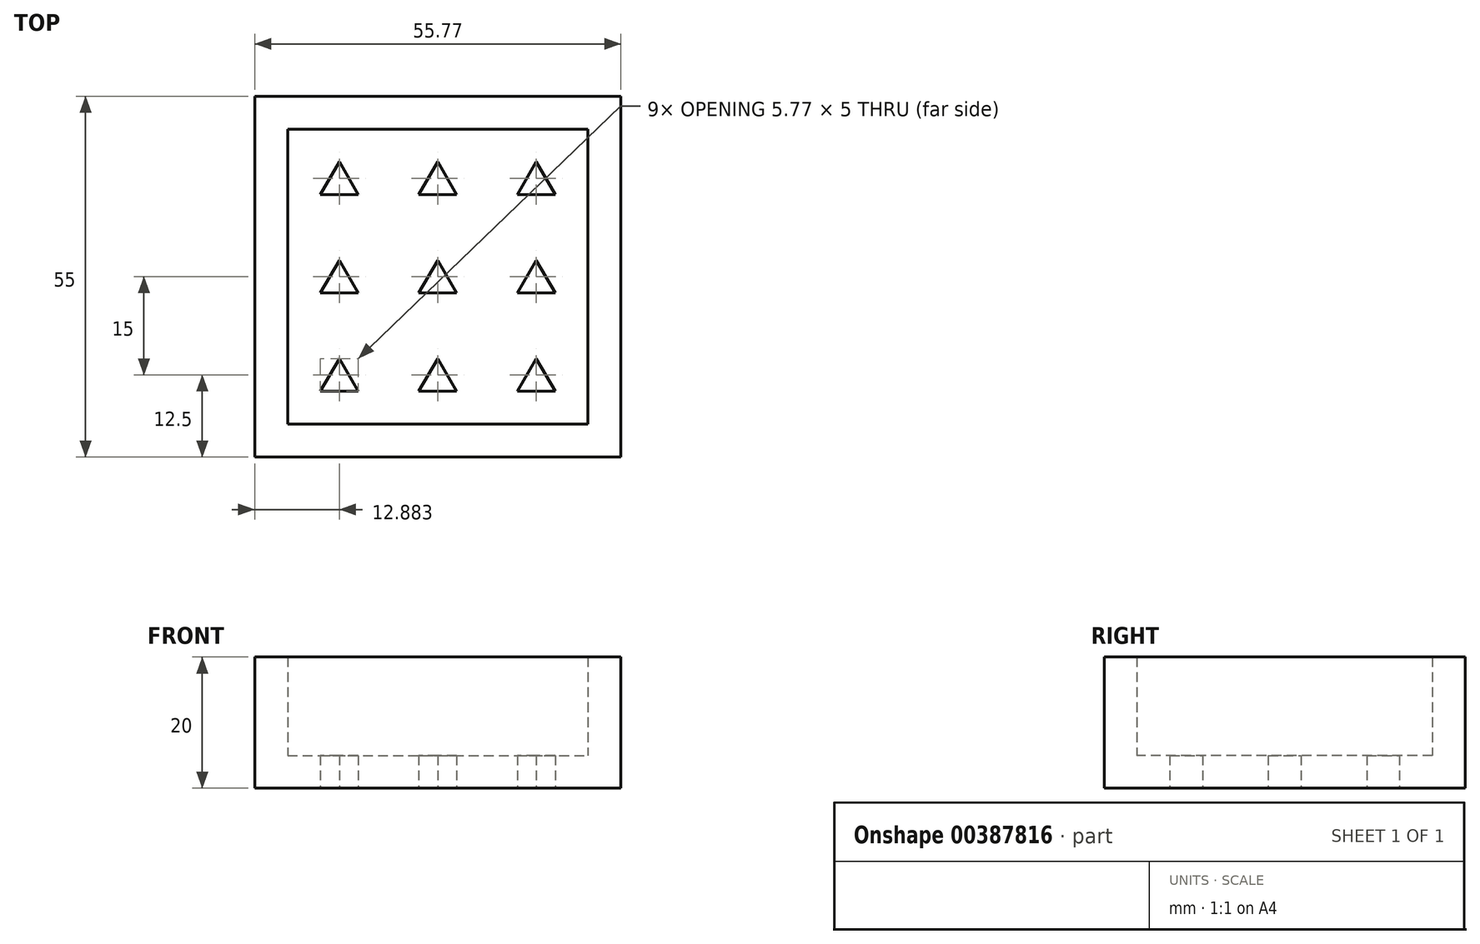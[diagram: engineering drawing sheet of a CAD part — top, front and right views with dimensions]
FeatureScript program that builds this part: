
annotation { "Feature Type Name" : "Feature", "Feature Type Description" : "" }
export const myFeature = defineFeature(function(context is Context, id is Id, definition is map)
    precondition{}
    {
        {
            var Q0;
            Q0=qCreatedBy(makeId("Top.planeOp"),FACE);
            var sketch = newSketch(context, id + "F0", { "sketchPlane" : qUnion([Q0])});
            skLineSegment(sketch, "E0", {"start": v(0, 0) * mm, "end": v(0, 0) * mm});
            skLineSegment(sketch, "E1", {"start": v(-2.89, 5) * mm, "end": v(-5.77, 0) * mm});
            skLineSegment(sketch, "E2", {"start": v(-5.77, 0) * mm, "end": v(0, 0) * mm});
            skLineSegment(sketch, "E3", {"start": v(0, 0) * mm, "end": v(-2.89, 5) * mm});
            skLineSegment(sketch, "E4.0.1.0", {"start": v(0, 15) * mm, "end": v(-2.89, 20) * mm});
            skLineSegment(sketch, "E4.0.1.1", {"start": v(-5.77, 15) * mm, "end": v(0, 15) * mm});
            skLineSegment(sketch, "E4.0.1.2", {"start": v(-2.89, 20) * mm, "end": v(-5.77, 15) * mm});
            skLineSegment(sketch, "E4.0.2.0", {"start": v(0, 30) * mm, "end": v(-2.89, 35) * mm});
            skLineSegment(sketch, "E4.0.2.1", {"start": v(-5.77, 30) * mm, "end": v(0, 30) * mm});
            skLineSegment(sketch, "E4.0.2.2", {"start": v(-2.89, 35) * mm, "end": v(-5.77, 30) * mm});
            skLineSegment(sketch, "E4.1.0.0", {"start": v(15, 0) * mm, "end": v(12.11, 5) * mm});
            skLineSegment(sketch, "E4.1.0.1", {"start": v(9.23, 0) * mm, "end": v(15, 0) * mm});
            skLineSegment(sketch, "E4.1.0.2", {"start": v(12.11, 5) * mm, "end": v(9.23, 0) * mm});
            skLineSegment(sketch, "E4.1.1.0", {"start": v(15, 15) * mm, "end": v(12.11, 20) * mm});
            skLineSegment(sketch, "E4.1.1.1", {"start": v(9.23, 15) * mm, "end": v(15, 15) * mm});
            skLineSegment(sketch, "E4.1.1.2", {"start": v(12.11, 20) * mm, "end": v(9.23, 15) * mm});
            skLineSegment(sketch, "E4.1.2.0", {"start": v(15, 30) * mm, "end": v(12.11, 35) * mm});
            skLineSegment(sketch, "E4.1.2.1", {"start": v(9.23, 30) * mm, "end": v(15, 30) * mm});
            skLineSegment(sketch, "E4.1.2.2", {"start": v(12.11, 35) * mm, "end": v(9.23, 30) * mm});
            skLineSegment(sketch, "E4.2.0.0", {"start": v(30, 0) * mm, "end": v(27.11, 5) * mm});
            skLineSegment(sketch, "E4.2.0.1", {"start": v(24.23, 0) * mm, "end": v(30, 0) * mm});
            skLineSegment(sketch, "E4.2.0.2", {"start": v(27.11, 5) * mm, "end": v(24.23, 0) * mm});
            skLineSegment(sketch, "E4.2.1.0", {"start": v(30, 15) * mm, "end": v(27.11, 20) * mm});
            skLineSegment(sketch, "E4.2.1.1", {"start": v(24.23, 15) * mm, "end": v(30, 15) * mm});
            skLineSegment(sketch, "E4.2.1.2", {"start": v(27.11, 20) * mm, "end": v(24.23, 15) * mm});
            skLineSegment(sketch, "E4.2.2.0", {"start": v(30, 30) * mm, "end": v(27.11, 35) * mm});
            skLineSegment(sketch, "E4.2.2.1", {"start": v(24.23, 30) * mm, "end": v(30, 30) * mm});
            skLineSegment(sketch, "E4.2.2.2", {"start": v(27.11, 35) * mm, "end": v(24.23, 30) * mm});
            skLineSegment(sketch, "E4.direction1", {"start": v(-5.77, 0) * mm, "end": v(9.23, 0) * mm, "construction": true});
            skLineSegment(sketch, "E4.direction2", {"start": v(-5.77, 0) * mm, "end": v(-5.77, 15) * mm, "construction": true});
            skLineSegment(sketch, "E5.bottom", {"start": v(-15.77, 45) * mm, "end": v(40, 45) * mm});
            skLineSegment(sketch, "E5.top", {"start": v(-15.77, -10) * mm, "end": v(40, -10) * mm});
            skLineSegment(sketch, "E5.left", {"start": v(-15.77, 45) * mm, "end": v(-15.77, -10) * mm});
            skLineSegment(sketch, "E5.right", {"start": v(40, 45) * mm, "end": v(40, -10) * mm});
            skSolve(sketch);
        }
        {
            var Q0;
            Q0 = qSketchRegion(id + "F0", true);
            extrude(context, id + "F1", {"entities" : qUnion([Q0]), "depth" : 5 * mm});
        }
        {
            var Q0;
            Q0=makeQuery(id+"F1.opExtrude","CAP_FACE",FACE,{"disambiguationData":[OSD([sQuery(id+"F0.wireOp",EDGE,"E1"),sQuery(id+"F0.wireOp",EDGE,"E2"),sQuery(id+"F0.wireOp",EDGE,"E3"),sQuery(id+"F0.wireOp",EDGE,"E4.0.1.0"),sQuery(id+"F0.wireOp",EDGE,"E4.0.1.1"),sQuery(id+"F0.wireOp",EDGE,"E4.0.1.2"),sQuery(id+"F0.wireOp",EDGE,"E4.0.2.0"),sQuery(id+"F0.wireOp",EDGE,"E4.0.2.1"),sQuery(id+"F0.wireOp",EDGE,"E4.0.2.2"),sQuery(id+"F0.wireOp",EDGE,"E4.1.0.0"),sQuery(id+"F0.wireOp",EDGE,"E4.1.0.1"),sQuery(id+"F0.wireOp",EDGE,"E4.1.0.2"),sQuery(id+"F0.wireOp",EDGE,"E4.1.1.0"),sQuery(id+"F0.wireOp",EDGE,"E4.1.1.1"),sQuery(id+"F0.wireOp",EDGE,"E4.1.1.2"),sQuery(id+"F0.wireOp",EDGE,"E4.1.2.0"),sQuery(id+"F0.wireOp",EDGE,"E4.1.2.1"),sQuery(id+"F0.wireOp",EDGE,"E4.1.2.2"),sQuery(id+"F0.wireOp",EDGE,"E4.2.0.0"),sQuery(id+"F0.wireOp",EDGE,"E4.2.0.1"),sQuery(id+"F0.wireOp",EDGE,"E4.2.0.2"),sQuery(id+"F0.wireOp",EDGE,"E4.2.1.0"),sQuery(id+"F0.wireOp",EDGE,"E4.2.1.1"),sQuery(id+"F0.wireOp",EDGE,"E4.2.1.2"),sQuery(id+"F0.wireOp",EDGE,"E4.2.2.0"),sQuery(id+"F0.wireOp",EDGE,"E4.2.2.1"),sQuery(id+"F0.wireOp",EDGE,"E4.2.2.2"),sQuery(id+"F0.wireOp",EDGE,"E5.bottom"),sQuery(id+"F0.wireOp",EDGE,"E5.top"),sQuery(id+"F0.wireOp",EDGE,"E5.left"),sQuery(id+"F0.wireOp",EDGE,"E5.right")])],"isStart":false});
            var sketch = newSketch(context, id + "F2", { "sketchPlane" : qUnion([Q0])});
            skLineSegment(sketch, "E6.0", {"start": v(-10.77, 40) * mm, "end": v(-10.77, -5) * mm});
            skLineSegment(sketch, "E6.1", {"start": v(35, 40) * mm, "end": v(-10.77, 40) * mm});
            skLineSegment(sketch, "E6.2", {"start": v(35, -5) * mm, "end": v(35, 40) * mm});
            skLineSegment(sketch, "E6.3", {"start": v(-10.77, -5) * mm, "end": v(35, -5) * mm});
            skSolve(sketch);
        }
        {
            var Q0;
            Q0=makeQuery(id+"F2.imprint","IMPRINT",FACE,{"disambiguationData":[TD([[makeQuery(id+"F2.imprint","IMPRINT",EDGE,{"derivedFrom":sQuery(id+"F2.wireOp",EDGE,"E6.0")}),-1.0]])]});
            extrude(context, id + "F3", {"entities" : qUnion([Q0]), "operationType" : NewBodyOperationType.ADD, "depth" : 15 * mm});
        }
    });
